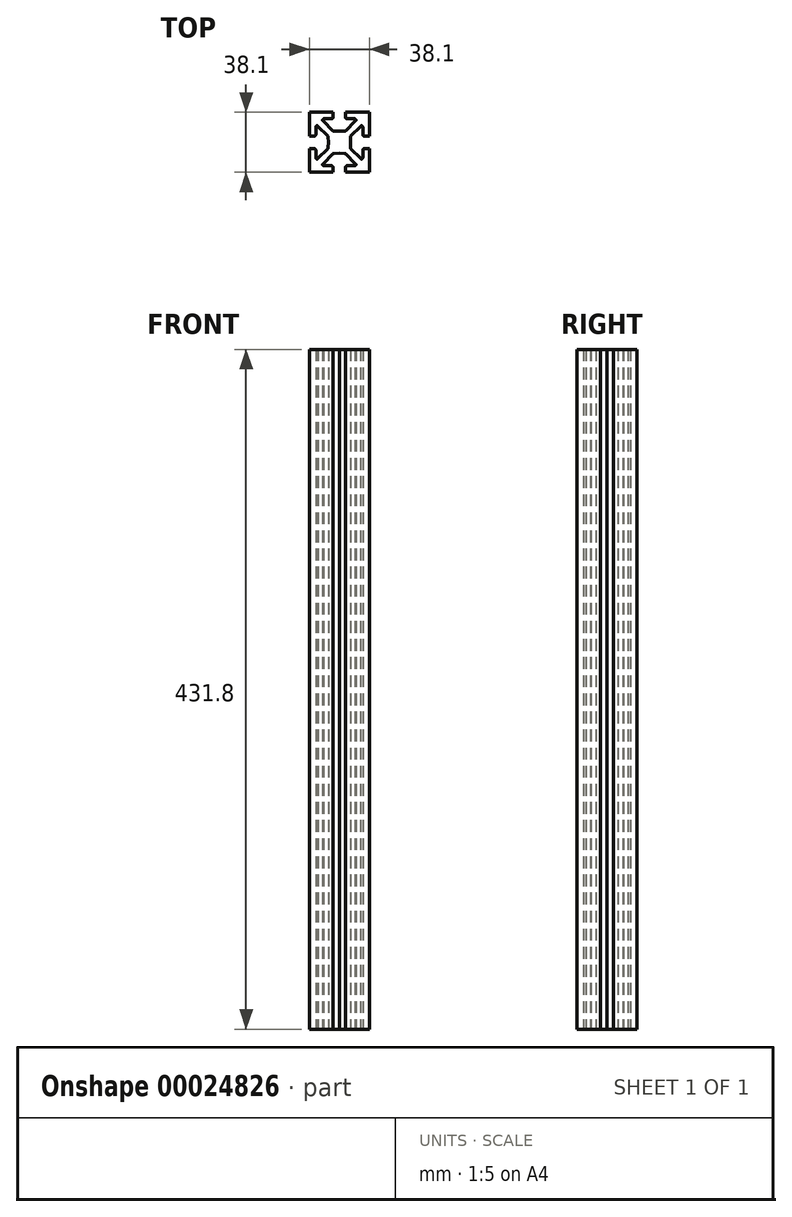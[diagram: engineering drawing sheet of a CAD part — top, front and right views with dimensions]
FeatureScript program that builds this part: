
annotation { "Feature Type Name" : "Feature", "Feature Type Description" : "" }
export const myFeature = defineFeature(function(context is Context, id is Id, definition is map)
    precondition{}
    {
        {
            var Q0;
            Q0=qCreatedBy(makeId("Front.planeOp"),FACE);
            var sketch = newSketch(context, id + "F0", { "sketchPlane" : qUnion([Q0])});
            skLineSegment(sketch, "E0.bottom", {"start": v(-19.05, 0) * mm, "end": v(19.05, 0) * mm});
            skLineSegment(sketch, "E0.top", {"start": v(-19.05, 431.8) * mm, "end": v(19.05, 431.8) * mm});
            skLineSegment(sketch, "E0.left", {"start": v(-19.05, 0) * mm, "end": v(-19.05, 431.8) * mm});
            skLineSegment(sketch, "E0.right", {"start": v(19.05, 0) * mm, "end": v(19.05, 431.8) * mm});
            skSolve(sketch);
        }
        {
            var Q0;
            Q0=makeQuery(id+"F0.imprint","IMPRINT",FACE,{"disambiguationData":[TD([[makeQuery(id+"F0.imprint","IMPRINT",EDGE,{"derivedFrom":sQuery(id+"F0.wireOp",EDGE,"E0.bottom")}),1.0]])]});
            extrude(context, id + "F1", {"entities" : qUnion([Q0]), "endBound" : BoundingType.SYMMETRIC, "depth" : 38.1 * mm});
        }
        {
            var Q0;
            Q0=qCreatedBy(makeId("Top.planeOp"),FACE);
            var sketch = newSketch(context, id + "F2", { "sketchPlane" : qUnion([Q0])});
            skLineSegment(sketch, "E1", {"start": v(-4.06, 19.11) * mm, "end": v(-4.06, 15.71) * mm});
            skLineSegment(sketch, "E2", {"start": v(-4.86, 14.92) * mm, "end": v(-9.78, 14.92) * mm});
            skLineSegment(sketch, "E3", {"start": v(0, 6.99) * mm, "end": v(0, 19.05) * mm});
            skLineSegment(sketch, "E4", {"start": v(0, 19.05) * mm, "end": v(-4.06, 19.11) * mm});
            skPoint(sketch, "E5.visualSharp", {"position": v(-10.29, 14.92) * mm});
            skArc(sketch, "E5.filletArc", {"start": v(-9.78, 14.92) * mm, "mid": v(-10.56, 14.3) * mm, "end": v(-10.12, 13.4) * mm});
            skPoint(sketch, "E6.visualSharp", {"position": v(-4.06, 14.92) * mm});
            skArc(sketch, "E6.filletArc", {"start": v(-4.86, 14.92) * mm, "mid": v(-4.3, 15.15) * mm, "end": v(-4.06, 15.71) * mm});
            skLineSegment(sketch, "E7", {"start": v(-10.12, 13.4) * mm, "end": v(-4.4, 7.51) * mm});
            skLineSegment(sketch, "E8", {"start": v(-3.28, 7.03) * mm, "end": v(0, 6.99) * mm});
            skPoint(sketch, "E9.visualSharp", {"position": v(-3.94, 7.04) * mm});
            skArc(sketch, "E9.filletArc", {"start": v(-4.4, 7.51) * mm, "mid": v(-3.89, 7.16) * mm, "end": v(-3.28, 7.03) * mm});
            skLineSegment(sketch, "E10.1.0", {"start": v(6.99, 0) * mm, "end": v(19.05, 0) * mm});
            skArc(sketch, "E10.1.1", {"start": v(7.51, 4.4) * mm, "mid": v(7.16, 3.89) * mm, "end": v(7.03, 3.28) * mm});
            skLineSegment(sketch, "E10.1.2", {"start": v(14.92, 4.86) * mm, "end": v(14.92, 9.78) * mm});
            skLineSegment(sketch, "E10.1.3", {"start": v(19.11, 4.06) * mm, "end": v(15.71, 4.06) * mm});
            skLineSegment(sketch, "E10.1.4", {"start": v(19.05, 0) * mm, "end": v(19.11, 4.06) * mm});
            skLineSegment(sketch, "E10.1.5", {"start": v(7.03, 3.28) * mm, "end": v(6.99, 0) * mm});
            skLineSegment(sketch, "E10.1.6", {"start": v(13.4, 10.12) * mm, "end": v(7.51, 4.4) * mm});
            skArc(sketch, "E10.1.7", {"start": v(14.92, 4.86) * mm, "mid": v(15.15, 4.3) * mm, "end": v(15.71, 4.06) * mm});
            skArc(sketch, "E10.1.8", {"start": v(14.92, 9.78) * mm, "mid": v(14.3, 10.56) * mm, "end": v(13.4, 10.12) * mm});
            skLineSegment(sketch, "E10.2.0", {"start": v(0, -6.99) * mm, "end": v(0, -19.05) * mm});
            skArc(sketch, "E10.2.1", {"start": v(4.4, -7.51) * mm, "mid": v(3.89, -7.16) * mm, "end": v(3.28, -7.03) * mm});
            skLineSegment(sketch, "E10.2.2", {"start": v(4.86, -14.92) * mm, "end": v(9.78, -14.92) * mm});
            skLineSegment(sketch, "E10.2.3", {"start": v(4.06, -19.11) * mm, "end": v(4.06, -15.71) * mm});
            skLineSegment(sketch, "E10.2.4", {"start": v(0, -19.05) * mm, "end": v(4.06, -19.11) * mm});
            skLineSegment(sketch, "E10.2.5", {"start": v(3.28, -7.03) * mm, "end": v(0, -6.99) * mm});
            skLineSegment(sketch, "E10.2.6", {"start": v(10.12, -13.4) * mm, "end": v(4.4, -7.51) * mm});
            skArc(sketch, "E10.2.7", {"start": v(4.86, -14.92) * mm, "mid": v(4.3, -15.15) * mm, "end": v(4.06, -15.71) * mm});
            skArc(sketch, "E10.2.8", {"start": v(9.78, -14.92) * mm, "mid": v(10.56, -14.3) * mm, "end": v(10.12, -13.4) * mm});
            skPoint(sketch, "E10.center", {"position": v(0, 0) * mm});
            skLineSegment(sketch, "E10.anchor1", {"start": v(0, 0) * mm, "end": v(-10.12, 13.4) * mm, "construction": true});
            skLineSegment(sketch, "E10.anchor2", {"start": v(0, 0) * mm, "end": v(-13.4, -10.12) * mm, "construction": true});
            skArc(sketch, "E11.3.3.0", {"start": v(-7.51, -4.4) * mm, "mid": v(-7.16, -3.89) * mm, "end": v(-7.03, -3.28) * mm});
            skLineSegment(sketch, "E11.7.3.0", {"start": v(-14.92, -4.86) * mm, "end": v(-14.92, -9.78) * mm});
            skLineSegment(sketch, "E11.10.3.0", {"start": v(-19.11, -4.06) * mm, "end": v(-15.71, -4.06) * mm});
            skLineSegment(sketch, "E11.13.3.0", {"start": v(-19.05, 0) * mm, "end": v(-19.11, -4.06) * mm});
            skLineSegment(sketch, "E11.16.3.0", {"start": v(-7.03, -3.28) * mm, "end": v(-6.99, 0) * mm});
            skLineSegment(sketch, "E11.19.3.0", {"start": v(-13.4, -10.12) * mm, "end": v(-7.51, -4.4) * mm});
            skLineSegment(sketch, "E11.20.3.0", {"start": v(-6.99, 0) * mm, "end": v(-19.05, 0) * mm});
            skArc(sketch, "E11.22.3.0", {"start": v(-14.92, -4.86) * mm, "mid": v(-15.15, -4.3) * mm, "end": v(-15.71, -4.06) * mm});
            skArc(sketch, "E11.26.3.0", {"start": v(-14.92, -9.78) * mm, "mid": v(-14.3, -10.56) * mm, "end": v(-13.4, -10.12) * mm});
            skArc(sketch, "E12.MirrorCS", {"start": v(4.4, 7.51) * mm, "mid": v(3.89, 7.16) * mm, "end": v(3.28, 7.03) * mm});
            skArc(sketch, "E13.MirrorCS", {"start": v(4.86, 14.92) * mm, "mid": v(4.3, 15.15) * mm, "end": v(4.06, 15.71) * mm});
            skArc(sketch, "E14.MirrorCS", {"start": v(9.78, 14.92) * mm, "mid": v(10.56, 14.3) * mm, "end": v(10.12, 13.4) * mm});
            skPoint(sketch, "E15.MirrorP", {"position": v(4.06, 14.92) * mm});
            skPoint(sketch, "E16.MirrorP", {"position": v(3.94, 7.04) * mm});
            skLineSegment(sketch, "E17.MirrorCS", {"start": v(3.28, 7.03) * mm, "end": v(0, 6.99) * mm});
            skLineSegment(sketch, "E18.MirrorCS", {"start": v(10.12, 13.4) * mm, "end": v(4.4, 7.51) * mm});
            skLineSegment(sketch, "E19.MirrorCS", {"start": v(0, 19.05) * mm, "end": v(4.06, 19.11) * mm});
            skLineSegment(sketch, "E20.MirrorCS", {"start": v(4.06, 19.11) * mm, "end": v(4.06, 15.71) * mm});
            skLineSegment(sketch, "E21.MirrorCS", {"start": v(4.86, 14.92) * mm, "end": v(9.78, 14.92) * mm});
            skPoint(sketch, "E22.MirrorP", {"position": v(10.29, 14.92) * mm});
            skArc(sketch, "E23.MirrorCS", {"start": v(-14.92, 9.78) * mm, "mid": v(-14.3, 10.56) * mm, "end": v(-13.4, 10.12) * mm});
            skArc(sketch, "E24.MirrorCS", {"start": v(-14.92, 4.86) * mm, "mid": v(-15.15, 4.3) * mm, "end": v(-15.71, 4.06) * mm});
            skLineSegment(sketch, "E25.MirrorCS", {"start": v(-19.05, 0) * mm, "end": v(-19.11, 4.06) * mm});
            skLineSegment(sketch, "E26.MirrorCS", {"start": v(-14.92, 4.86) * mm, "end": v(-14.92, 9.78) * mm});
            skLineSegment(sketch, "E27.MirrorCS", {"start": v(-19.11, 4.06) * mm, "end": v(-15.71, 4.06) * mm});
            skArc(sketch, "E28.MirrorCS", {"start": v(-7.51, 4.4) * mm, "mid": v(-7.16, 3.89) * mm, "end": v(-7.03, 3.28) * mm});
            skLineSegment(sketch, "E29.MirrorCS", {"start": v(-13.4, 10.12) * mm, "end": v(-7.51, 4.4) * mm});
            skLineSegment(sketch, "E30.MirrorCS", {"start": v(-7.03, 3.28) * mm, "end": v(-6.99, 0) * mm});
            skLineSegment(sketch, "E31.MirrorCS", {"start": v(19.05, 0) * mm, "end": v(19.11, -4.06) * mm});
            skArc(sketch, "E32.MirrorCS", {"start": v(14.92, -4.86) * mm, "mid": v(15.15, -4.3) * mm, "end": v(15.71, -4.06) * mm});
            skLineSegment(sketch, "E33.MirrorCS", {"start": v(19.11, -4.06) * mm, "end": v(15.71, -4.06) * mm});
            skLineSegment(sketch, "E34.MirrorCS", {"start": v(7.03, -3.28) * mm, "end": v(6.99, 0) * mm});
            skArc(sketch, "E35.MirrorCS", {"start": v(7.51, -4.4) * mm, "mid": v(7.16, -3.89) * mm, "end": v(7.03, -3.28) * mm});
            skLineSegment(sketch, "E36.MirrorCS", {"start": v(14.92, -4.86) * mm, "end": v(14.92, -9.78) * mm});
            skLineSegment(sketch, "E37.MirrorCS", {"start": v(13.4, -10.12) * mm, "end": v(7.51, -4.4) * mm});
            skArc(sketch, "E38.MirrorCS", {"start": v(14.92, -9.78) * mm, "mid": v(14.3, -10.56) * mm, "end": v(13.4, -10.12) * mm});
            skLineSegment(sketch, "E39.MirrorCS", {"start": v(0, -19.05) * mm, "end": v(-4.06, -19.11) * mm});
            skLineSegment(sketch, "E40.MirrorCS", {"start": v(-4.06, -19.11) * mm, "end": v(-4.06, -15.71) * mm});
            skArc(sketch, "E41.MirrorCS", {"start": v(-4.86, -14.92) * mm, "mid": v(-4.3, -15.15) * mm, "end": v(-4.06, -15.71) * mm});
            skLineSegment(sketch, "E42.MirrorCS", {"start": v(-4.86, -14.92) * mm, "end": v(-9.78, -14.92) * mm});
            skArc(sketch, "E43.MirrorCS", {"start": v(-9.78, -14.92) * mm, "mid": v(-10.56, -14.3) * mm, "end": v(-10.12, -13.4) * mm});
            skLineSegment(sketch, "E44.MirrorCS", {"start": v(-3.28, -7.03) * mm, "end": v(0, -6.99) * mm});
            skLineSegment(sketch, "E45.MirrorCS", {"start": v(-10.12, -13.4) * mm, "end": v(-4.4, -7.51) * mm});
            skArc(sketch, "E46.MirrorCS", {"start": v(-4.4, -7.51) * mm, "mid": v(-3.89, -7.16) * mm, "end": v(-3.28, -7.03) * mm});
            skSolve(sketch);
        }
        {
            var Q0;
            Q0 = qSketchRegion(id + "F2", true);
            extrude(context, id + "F3", {"entities" : qUnion([Q0]), "operationType" : NewBodyOperationType.REMOVE, "endBound" : BoundingType.UP_TO_NEXT, "depth" : 25.4 * mm});
        }
    });
